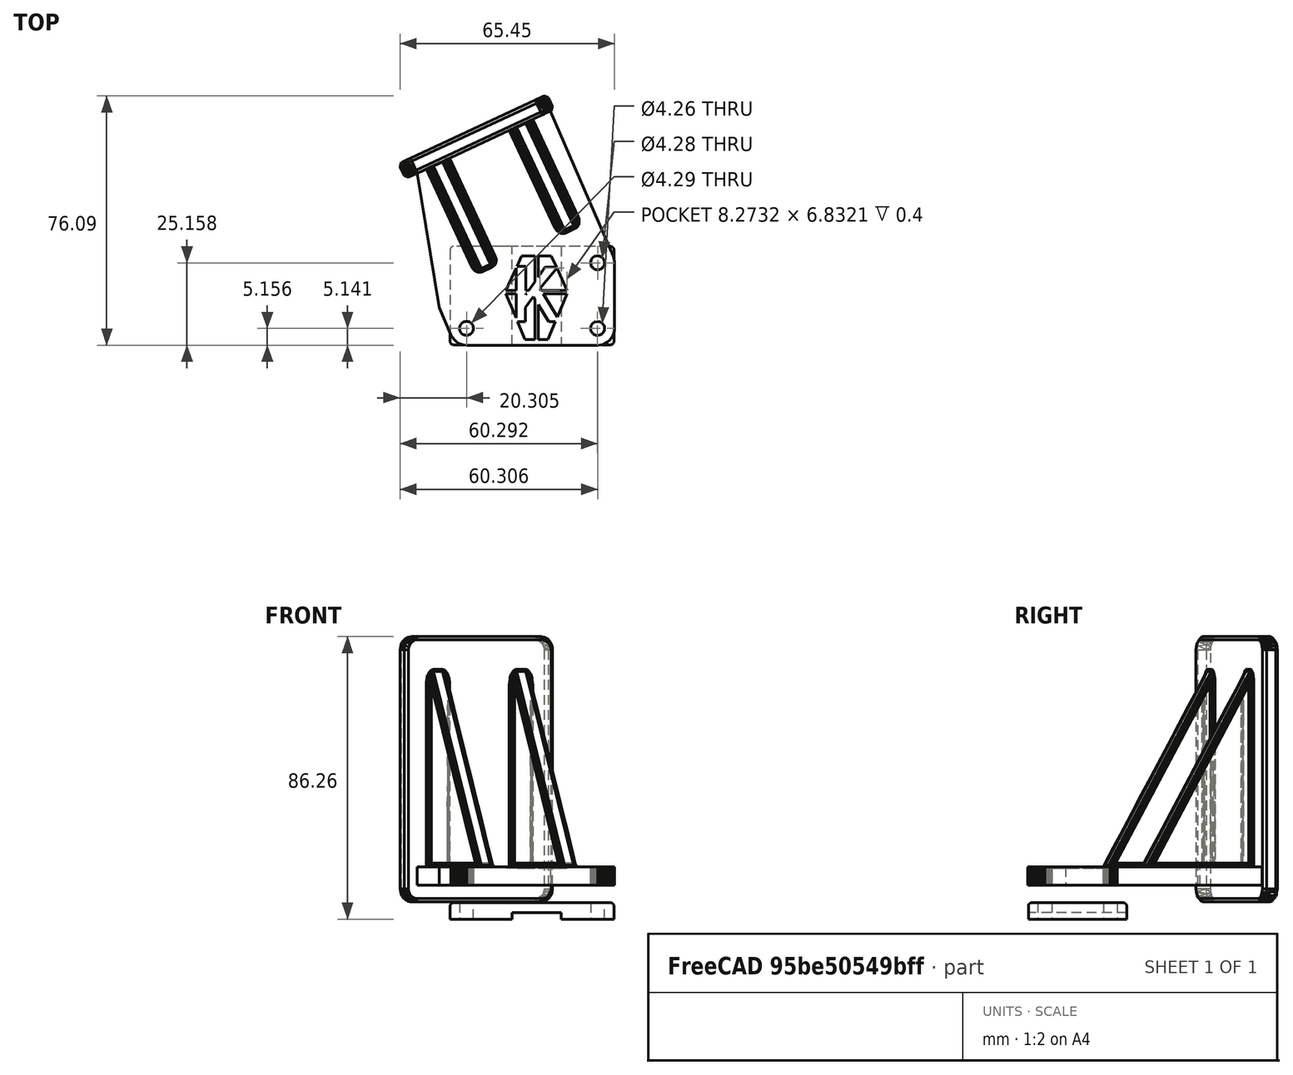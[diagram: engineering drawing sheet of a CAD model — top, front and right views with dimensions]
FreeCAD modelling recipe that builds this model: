
FCSTD DOCUMENT  (FreeCAD 1.1R14555 (Git shallow))
Label: Remix Nebula Mount
License: All rights reserved
LicenseURL: https://en.wikipedia.org/wiki/All_rights_reserved
objects: Sketcher::SketchObject×3, App::Point×2, PartDesign::Pocket×2, PartDesign::Body×2, PartDesign::Fillet×2, Mesh::Feature×1, Part::Feature×1, Part::Refine×1, PartDesign::FeatureBase×1, PartDesign::SubShapeBinder×1, PartDesign::Pad×1
note: 28 computed .brp shape members not serialized (recipe doc carries the construction recipe); baked Part::Feature solids carry a one-line shape summary decoded from their .brp

FEATURE [Mesh::Feature] Nebula_Mount_Landscape_v2  label="Nebula Mount Landscape v2"
FEATURE [Part::Feature] Nebula_Mount_Landscape_v001
  shape: bbox 65.46 x 76.09 x 81 mm, 4686 faces, 0 solids (baked)
FEATURE [Part::Refine] Nebula_Mount_Landscape_v002
  Source = -> Nebula_Mount_Landscape_v001
FEATURE [App::Point] Origin001
  Role = Origin
FEATURE [PartDesign::FeatureBase] BaseFeature
  BaseFeature = -> Nebula_Mount_Landscape_v002
  Suppressed = false
FEATURE [Sketcher::SketchObject] Sketch
  ArcFitTolerance = 1e-06
  AttachmentSupport = -> [BaseFeature]
  ExternalGeometry = -> [BaseFeature]
  ExternalTypes = [0,0,0,0,0,0,0,0]
  FullyConstrained = false
  MakeInternals = false
  MapMode = 5
  Placement = pos=(-27.678,59.3584,0.000485333) rot=(-0.154865,0.698573,0.698579;3.44888rad)
  sketch-geometry (4):
    g0: Circle [constr] CenterX=-9.04763 CenterY=72.2149 CenterZ=0 NormalX=0 NormalY=0 NormalZ=1 AngleXU=0 Radius=2.63777
    g1: Circle [constr] CenterX=-9.06482 CenterY=40.2035 CenterZ=0 NormalX=0 NormalY=0 NormalZ=1 AngleXU=0 Radius=2.63777
    g2: Circle CenterX=-9.04763 CenterY=72.2149 CenterZ=0 NormalX=0 NormalY=0 NormalZ=1 AngleXU=0 Radius=4
    g3: Circle CenterX=-9.06482 CenterY=40.2035 CenterZ=0 NormalX=0 NormalY=0 NormalZ=1 AngleXU=0 Radius=4
  constraints (7):
    c: PointOnObject(g-7,g0)
    c: PointOnObject(g-5,g1)
    c: Equal(g0,g1)
    c: Coincident(g2,g0)
    c: Coincident(g3,g1)
    c: Equal(g2,g3)
    c: Diameter(g2) = 8
FEATURE [PartDesign::Pocket] Pocket
  BaseFeature = -> BaseFeature
  Direction = (0.42,-0.91,0)
  Length = 5
  Length2 = 5
  Profile = -> Sketch
  ReferenceAxis = -> Sketch [N_Axis]
  Refine = true
  Reversed = true
  Suppressed = false
  Type = 0
FEATURE [PartDesign::Body] Body
  AllowCompound = false
  BaseFeature = -> Nebula_Mount_Landscape_v002
  Group = -> [BaseFeature,Sketch,Pocket]
  Origin = -> Origin
  Tip = -> Pocket
FEATURE [App::Point] Origin003
  Role = Origin
FEATURE [PartDesign::SubShapeBinder] Binder
  BindCopyOnChange = 0
  BindMode = 0
  ClaimChildren = false
  Context = -> Body001 [Binder.]
  Fuse = false
  MakeFace = true
  OffsetFill = false
  OffsetIntersection = false
  OffsetJoinType = 0
  OffsetOpenResult = false
  PartialLoad = false
  Refine = true
  Relative = true
  Support = -> [Nebula_Mount_Landscape_v002]
  _Version = 2
FEATURE [Sketcher::SketchObject] Sketch001
  ArcFitTolerance = 1e-06
  AttachmentSupport = -> [Origin002]
  ExternalGeometry = -> [Binder]
  ExternalTypes = [0,0,0,0,0,0,0,0,0]
  FullyConstrained = true
  MakeInternals = false
  MapMode = 5
  sketch-geometry (7):
    g0: Circle CenterX=-21.3649 CenterY=2.40628 CenterZ=0 NormalX=0 NormalY=0 NormalZ=1 AngleXU=0 Radius=2.14311
    g1: Circle CenterX=18.6365 CenterY=22.4083 CenterZ=0 NormalX=0 NormalY=0 NormalZ=1 AngleXU=0 Radius=2.14132
    g2: Circle CenterX=18.6217 CenterY=2.39123 CenterZ=0 NormalX=0 NormalY=0 NormalZ=1 AngleXU=0 Radius=2.1324
    g3: LineSegment StartX=23.6217 StartY=27.3912 StartZ=0 EndX=-26.3649 EndY=27.3912 EndZ=0
    g4: LineSegment StartX=-26.3649 StartY=27.3912 StartZ=0 EndX=-26.3649 EndY=-2.60877 EndZ=0
    g5: LineSegment StartX=-26.3649 StartY=-2.60877 StartZ=0 EndX=23.6217 EndY=-2.60877 EndZ=0
    g6: LineSegment StartX=23.6217 StartY=-2.60877 StartZ=0 EndX=23.6217 EndY=27.3912 EndZ=0
  constraints (21):
    c: PointOnObject(g-5,g0)
    c: PointOnObject(g-3,g0)
    c: PointOnObject(g-4,g0)
    c: PointOnObject(g-6,g1)
    c: PointOnObject(g-7,g1)
    c: PointOnObject(g-8,g1)
    c: PointOnObject(g-9,g2)
    c: PointOnObject(g-10,g2)
    c: PointOnObject(g-11,g2)
    c: Coincident(g3,g4)
    c: Coincident(g4,g5)
    c: Coincident(g5,g6)
    c: Coincident(g6,g3)
    c: Horizontal(g3)
    c: Horizontal(g5)
    c: Vertical(g4)
    c: Vertical(g6)
    c: DistanceY(g6,g6) = 30
    c: DistanceX(g2,g5) = 5
    c: DistanceX(g4,g0) = 5
    c: DistanceY(g5,g2) = 5
FEATURE [PartDesign::Pad] Pad
  Direction = (0,0,1)
  Length = 5
  Length2 = 10
  Profile = -> Sketch001
  ReferenceAxis = -> Sketch001 [N_Axis]
  Refine = true
  Suppressed = false
  Type = 0
FEATURE [Sketcher::SketchObject] Sketch002
  ArcFitTolerance = 1e-06
  AttachmentSupport = -> [Pad]
  ExternalTypes = [0,0]
  FullyConstrained = false
  MakeInternals = false
  MapMode = 5
  Placement = pos=(0,0,0) rot=(1,0,0;3.14159rad)
  sketch-geometry (4):
    g0: LineSegment StartX=-7.5 StartY=4.37518 StartZ=0 EndX=-7.5 EndY=-29.4276 EndZ=0
    g1: LineSegment StartX=-7.5 StartY=-29.4276 StartZ=0 EndX=7.5 EndY=-29.4276 EndZ=0
    g2: LineSegment StartX=7.5 StartY=-29.4276 StartZ=0 EndX=7.5 EndY=4.37518 EndZ=0
    g3: LineSegment StartX=7.5 StartY=4.37518 StartZ=0 EndX=-7.5 EndY=4.37518 EndZ=0
  constraints (9):
    c: Coincident(g0,g1)
    c: Coincident(g1,g2)
    c: Coincident(g2,g3)
    c: Coincident(g3,g0)
    c: Vertical(g0)
    c: Vertical(g2)
    c: Horizontal(g1)
    c: DistanceX(g3,g3) = 15
    c: Symmetric(g0,g2,g-2)
FEATURE [PartDesign::Pocket] Pocket001
  BaseFeature = -> Pad
  Direction = (0,0,1)
  Length = 2
  Length2 = 5
  Profile = -> Sketch002
  ReferenceAxis = -> Sketch002 [N_Axis]
  Refine = true
  Suppressed = false
  Type = 0
FEATURE [PartDesign::Fillet] Fillet
  Base = -> Pocket001 [Edge8,Edge6,Edge23,Edge30]
  BaseFeature = -> Pocket001
  Radius = 1
  Refine = true
  SupportTransform = false
  Suppressed = false
  UseAllEdges = false
FEATURE [PartDesign::Fillet] Fillet001
  Base = -> Fillet [Edge4,Edge20,Edge22,Edge24,Edge25,Edge23,Edge21,Edge17]
  BaseFeature = -> Fillet
  Radius = 1
  Refine = true
  SupportTransform = false
  Suppressed = false
  UseAllEdges = false
FEATURE [PartDesign::Body] Body001
  AllowCompound = true
  Group = -> [Sketch001,Binder,Pad,Sketch002,Pocket001,Fillet,Fillet001]
  Origin = -> Origin002
  Tip = -> Fillet001
